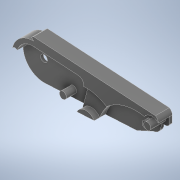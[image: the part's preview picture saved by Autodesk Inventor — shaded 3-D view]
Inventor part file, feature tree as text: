
AUTODESK INVENTOR PART (.ipt)
format: ipt  version: 2022 (Build 260153000, 153)  size: 455,680 bytes
history: native  units: in
note: dims shown in document units (in); Inventor stores cm internally (conversion verified against a paired STEP export)
features: extrude x7, sketch x7, other x1
ambient origin geometry x8: Origin, YZ Plane, XZ Plane, XY Plane, X Axis, Y Axis, Z Axis, Center Point
bodies: Body1 (feature_tree)
feature tree (15):
  other  "Sólido1"
  extrude  "Extrusión1"  Depth=0.0984in
  extrude  "Extrusión2"  Depth=0.5906in
  extrude  "Extrusión3"  Depth=0.0984in
  extrude  "Extrusión6"  Depth=0.1181in
  extrude  "Extrusión7"  Depth=0.0984in
  extrude  "Extrusión10"  Depth=0.0787in
  extrude  "Extrusión11"  Depth=0.0197in
  sketch  "Boceto1"  dims[d9=0.0984in d10=0.0984in]
  sketch  "Boceto2"  dims[d11=1.5354in d12=0.5906in]
  sketch  "Boceto3"  dims[d13=0.2362in d14=0.0984in]
  sketch  "Boceto7"  dims[d15=0.1378in d16=0.1181in]
  sketch  "Boceto8"  dims[d17=0.1575in d18=0.0984in]
  sketch  "Boceto11"  dims[d19=0.128in d20=0.0787in]
  sketch  "Boceto12"  dims[d21=0.0787in d22=0.2205in d23=0.2244in d25=0.0394in d26=0.0in d27=0.0787in d28=0.0in d31=0.2165in d32=0.0in d35=0.0984in d36=0.0787in d39=0.0984in d40=0.0984in d41=0.0591in d42=0.0in d43=0.0315in d44=0.0in d55=0.0787in d56=0.0787in d57=0.0in d59=0.0394in d60=0.0in d33=0.0197in d34=0.0344in d61=0.0197in d62=0.0344in]
